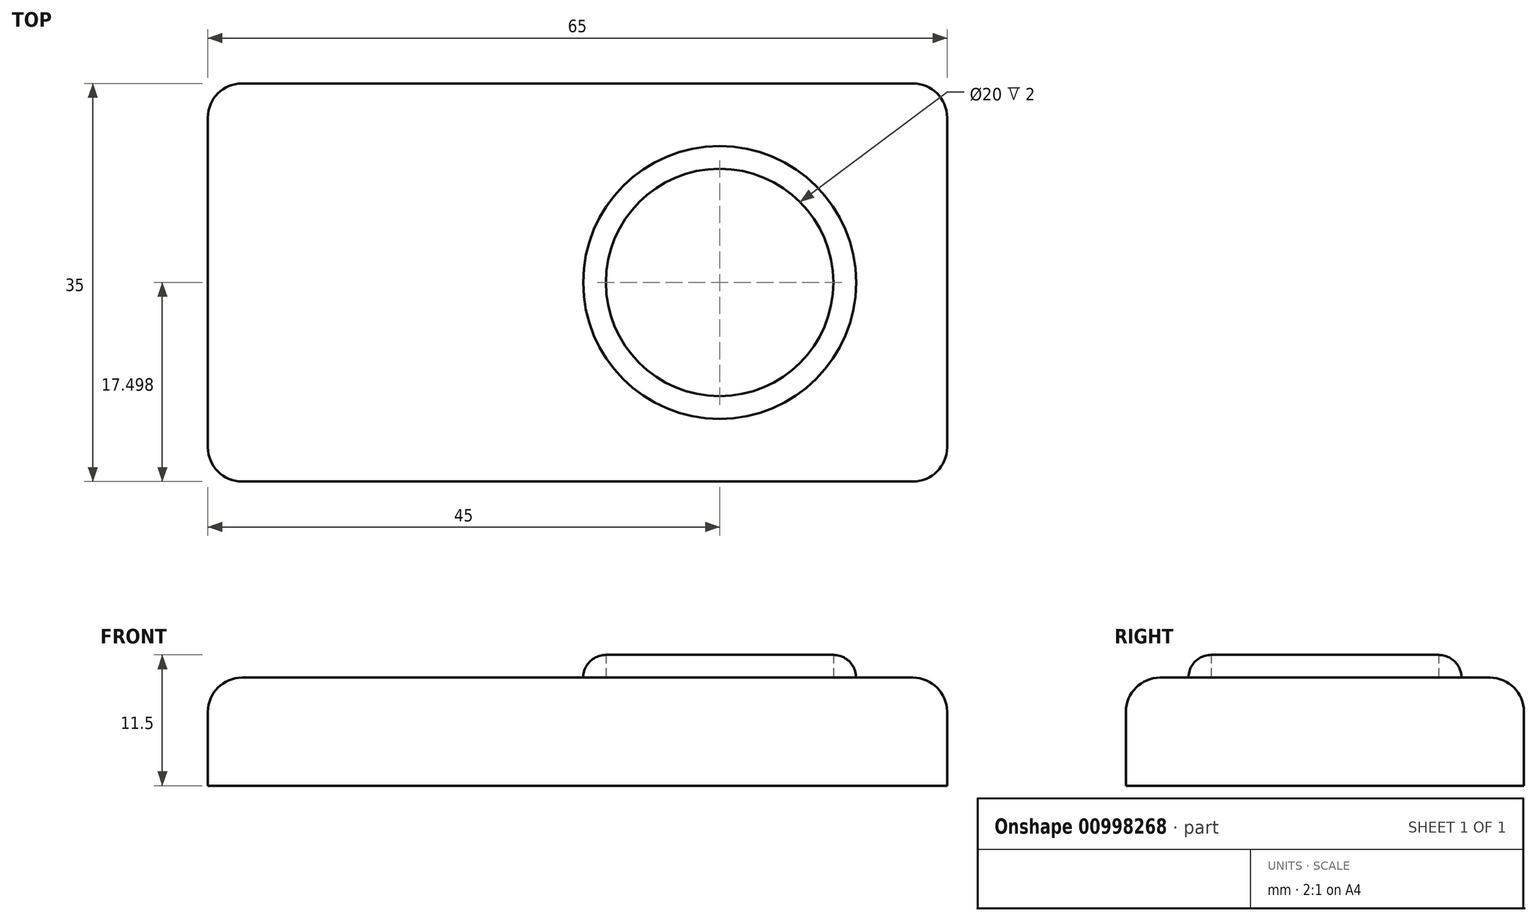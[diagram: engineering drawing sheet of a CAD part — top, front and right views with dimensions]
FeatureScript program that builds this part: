
annotation { "Feature Type Name" : "Feature", "Feature Type Description" : "" }
export const myFeature = defineFeature(function(context is Context, id is Id, definition is map)
    precondition{}
    {
        {
            var Q0;
            Q0=qCreatedBy(makeId("Top.planeOp"),FACE);
            var sketch = newSketch(context, id + "F0", { "sketchPlane" : qUnion([Q0])});
            skLineSegment(sketch, "E0.bottom", {"start": v(-38.2, 5.28) * mm, "end": v(26.8, 5.28) * mm});
            skLineSegment(sketch, "E0.top", {"start": v(-38.2, -29.72) * mm, "end": v(26.8, -29.72) * mm});
            skLineSegment(sketch, "E0.left", {"start": v(-38.2, 5.28) * mm, "end": v(-38.2, -29.72) * mm});
            skLineSegment(sketch, "E0.right", {"start": v(26.8, 5.28) * mm, "end": v(26.8, -29.72) * mm});
            skLineSegment(sketch, "E1", {"start": v(26.8, 5.28) * mm, "end": v(6.8, 5.28) * mm});
            skLineSegment(sketch, "E2", {"start": v(6.8, 5.28) * mm, "end": v(6.8, -29.72) * mm});
            skCircle(sketch, "E3", {"center": v(6.8, -12.22) * mm, "radius": 10 * mm});
            skLineSegment(sketch, "E4", {"start": v(26.8, -12.22) * mm, "end": v(16.8, -12.22) * mm});
            skCircle(sketch, "E5", {"center": v(6.8, -12.22) * mm, "radius": 12 * mm});
            skSolve(sketch);
        }
        {
            var Q0;
            {var subQ5=sQuery(id+"F0.wireOp",EDGE,"E0.left");Q0=makeQuery(id+"F0.imprint","IMPRINT",FACE,{"disambiguationData":[TD([[makeQuery(id+"F0.imprint","IMPRINT",EDGE,{"derivedFrom":subQ5}),1.0]])]});}
            var Q1;
            {var subQ1=sQuery(id+"F0.wireOp",EDGE,"E0.right");var subQ6=sQuery(id+"F0.wireOp",EDGE,"E0.bottom");var subQ9=makeQuery(id+"F0.imprint","INTERSECT",VERTEX,{"derivedFrom":[subQ6,subQ1]});Q1=makeQuery(id+"F0.imprint","IMPRINT",FACE,{"disambiguationData":[TD([[makeQuery(id+"F0.imprint","IMPRINT",EDGE,{"disambiguationData":[TD([[subQ9,1.0]])],"derivedFrom":subQ6}),-1.0]])]});}
            var Q2;
            {var subQ1=sQuery(id+"F0.wireOp",EDGE,"E0.right");var subQ5=sQuery(id+"F0.wireOp",EDGE,"E0.top");var subQ6=makeQuery(id+"F0.imprint","INTERSECT",VERTEX,{"derivedFrom":[subQ5,subQ1]});Q2=makeQuery(id+"F0.imprint","IMPRINT",FACE,{"disambiguationData":[TD([[makeQuery(id+"F0.imprint","IMPRINT",EDGE,{"disambiguationData":[TD([[subQ6,1.0]])],"derivedFrom":subQ5}),1.0]])]});}
            var Q3;
            {var subQ0=sQuery(id+"F0.wireOp",EDGE,"E3");var subQ1=sQuery(id+"F0.wireOp",EDGE,"E2");var subQ2=makeQuery(id+"F0.imprint","INTERSECT",VERTEX,{"disambiguationData":[OD(1.0)],"derivedFrom":[subQ1,subQ0]});Q3=makeQuery(id+"F0.imprint","IMPRINT",FACE,{"disambiguationData":[TD([[makeQuery(id+"F0.imprint","IMPRINT",EDGE,{"disambiguationData":[TD([[subQ2,-1.0]])],"derivedFrom":subQ1}),1.0]])]});}
            var Q4;
            {var subQ0=sQuery(id+"F0.wireOp",EDGE,"E3");var subQ1=sQuery(id+"F0.wireOp",EDGE,"E2");var subQ2=makeQuery(id+"F0.imprint","INTERSECT",VERTEX,{"disambiguationData":[OD(0.0)],"derivedFrom":[subQ1,subQ0]});Q4=makeQuery(id+"F0.imprint","IMPRINT",FACE,{"disambiguationData":[TD([[makeQuery(id+"F0.imprint","IMPRINT",EDGE,{"disambiguationData":[TD([[subQ2,1.0]])],"derivedFrom":subQ1}),1.0]])]});}
            var Q5;
            {var subQ0=sQuery(id+"F0.wireOp",EDGE,"E3");var subQ1=sQuery(id+"F0.wireOp",EDGE,"E2");var subQ2=makeQuery(id+"F0.imprint","INTERSECT",VERTEX,{"disambiguationData":[OD(1.0)],"derivedFrom":[subQ1,subQ0]});Q5=makeQuery(id+"F0.imprint","IMPRINT",FACE,{"disambiguationData":[TD([[makeQuery(id+"F0.imprint","IMPRINT",EDGE,{"disambiguationData":[TD([[subQ2,-1.0]])],"derivedFrom":subQ1}),-1.0]])]});}
            var Q6;
            {var subQ0=sQuery(id+"F0.wireOp",EDGE,"E3");var subQ1=sQuery(id+"F0.wireOp",EDGE,"E2");var subQ2=makeQuery(id+"F0.imprint","INTERSECT",VERTEX,{"disambiguationData":[OD(0.0)],"derivedFrom":[subQ1,subQ0]});Q6=makeQuery(id+"F0.imprint","IMPRINT",FACE,{"disambiguationData":[TD([[makeQuery(id+"F0.imprint","IMPRINT",EDGE,{"disambiguationData":[TD([[subQ2,-1.0]])],"derivedFrom":subQ1}),-1.0]])]});}
            var Q7;
            {var subQ0=sQuery(id+"F0.wireOp",EDGE,"E3");var subQ1=sQuery(id+"F0.wireOp",EDGE,"E2");var subQ2=makeQuery(id+"F0.imprint","INTERSECT",VERTEX,{"disambiguationData":[OD(0.0)],"derivedFrom":[subQ1,subQ0]});Q7=makeQuery(id+"F0.imprint","IMPRINT",FACE,{"disambiguationData":[TD([[makeQuery(id+"F0.imprint","IMPRINT",EDGE,{"disambiguationData":[TD([[subQ2,-1.0]])],"derivedFrom":subQ1}),1.0]])]});}
            extrude(context, id + "F1", {"entities" : qUnion([Q0, Q1, Q2, Q3, Q4, Q5, Q6, Q7]), "depth" : 9.5 * mm, "offsetDistance" : 25 * mm});
        }
        {
            var Q0;
            {var subQ0=sQuery(id+"F0.wireOp",EDGE,"E3");var subQ1=sQuery(id+"F0.wireOp",EDGE,"E2");var subQ2=makeQuery(id+"F0.imprint","INTERSECT",VERTEX,{"disambiguationData":[OD(1.0)],"derivedFrom":[subQ1,subQ0]});Q0=makeQuery(id+"F0.imprint","IMPRINT",FACE,{"disambiguationData":[TD([[makeQuery(id+"F0.imprint","IMPRINT",EDGE,{"disambiguationData":[TD([[subQ2,-1.0]])],"derivedFrom":subQ1}),1.0]])]});}
            var Q1;
            {var subQ0=sQuery(id+"F0.wireOp",EDGE,"E3");var subQ1=sQuery(id+"F0.wireOp",EDGE,"E2");var subQ2=makeQuery(id+"F0.imprint","INTERSECT",VERTEX,{"disambiguationData":[OD(0.0)],"derivedFrom":[subQ1,subQ0]});Q1=makeQuery(id+"F0.imprint","IMPRINT",FACE,{"disambiguationData":[TD([[makeQuery(id+"F0.imprint","IMPRINT",EDGE,{"disambiguationData":[TD([[subQ2,1.0]])],"derivedFrom":subQ1}),1.0]])]});}
            var Q2;
            {var subQ0=sQuery(id+"F0.wireOp",EDGE,"E3");var subQ1=sQuery(id+"F0.wireOp",EDGE,"E2");var subQ2=makeQuery(id+"F0.imprint","INTERSECT",VERTEX,{"disambiguationData":[OD(1.0)],"derivedFrom":[subQ1,subQ0]});Q2=makeQuery(id+"F0.imprint","IMPRINT",FACE,{"disambiguationData":[TD([[makeQuery(id+"F0.imprint","IMPRINT",EDGE,{"disambiguationData":[TD([[subQ2,-1.0]])],"derivedFrom":subQ1}),-1.0]])]});}
            extrude(context, id + "F2", {"entities" : qUnion([Q0, Q1, Q2]), "operationType" : NewBodyOperationType.ADD, "depth" : 11.5 * mm, "offsetDistance" : 25 * mm});
        }
        {
            var Q0;
            Q0=makeQuery(id+"F2.opExtrude","CAP_EDGE",EDGE,{"disambiguationData":[OSD([sQuery(id+"F0.wireOp",EDGE,"E5")])],"isStart":false});
            fillet(context, id + "F3", {"entities" : qUnion([Q0]), "radius" : 2 * mm, "tangentPropagation" : true, "allowEdgeOverflow" : false});
        }
        {
            var Q0;
            Q0=makeQuery(id+"F1.opExtrude","CAP_EDGE",EDGE,{"disambiguationData":[OSD([sQuery(id+"F0.wireOp",EDGE,"E0.top")])],"isStart":false});
            var Q1;
            Q1=makeQuery(id+"F1.opExtrude","CAP_EDGE",EDGE,{"disambiguationData":[OSD([sQuery(id+"F0.wireOp",EDGE,"E0.right")])],"isStart":false});
            var Q2;
            Q2=makeQuery(id+"F1.opExtrude","SWEPT_EDGE",EDGE,{"disambiguationData":[OSD([sQuery(id+"F0.wireOp",EDGE,"E0.top"),sQuery(id+"F0.wireOp",EDGE,"E0.right")])]});
            var Q3;
            Q3=makeQuery(id+"F1.opExtrude","SWEPT_EDGE",EDGE,{"disambiguationData":[OSD([sQuery(id+"F0.wireOp",EDGE,"E0.top"),sQuery(id+"F0.wireOp",EDGE,"E0.left")])]});
            var Q4;
            Q4=makeQuery(id+"F1.opExtrude","CAP_EDGE",EDGE,{"disambiguationData":[OSD([sQuery(id+"F0.wireOp",EDGE,"E0.left")])],"isStart":false});
            var Q5;
            Q5=makeQuery(id+"F1.opExtrude","SWEPT_EDGE",EDGE,{"disambiguationData":[OSD([sQuery(id+"F0.wireOp",EDGE,"E0.bottom"),sQuery(id+"F0.wireOp",EDGE,"E0.left")])]});
            var Q6;
            Q6=makeQuery(id+"F1.opExtrude","SWEPT_EDGE",EDGE,{"disambiguationData":[OSD([sQuery(id+"F0.wireOp",EDGE,"E0.bottom"),sQuery(id+"F0.wireOp",EDGE,"E0.right")])]});
            var Q7;
            Q7=makeQuery(id+"F1.opExtrude","CAP_EDGE",EDGE,{"disambiguationData":[OSD([sQuery(id+"F0.wireOp",EDGE,"E0.bottom")])],"isStart":false});
            fillet(context, id + "F4", {"entities" : qUnion([Q0, Q1, Q2, Q3, Q4, Q5, Q6, Q7]), "radius" : 3 * mm, "tangentPropagation" : true, "allowEdgeOverflow" : false});
        }
    });
